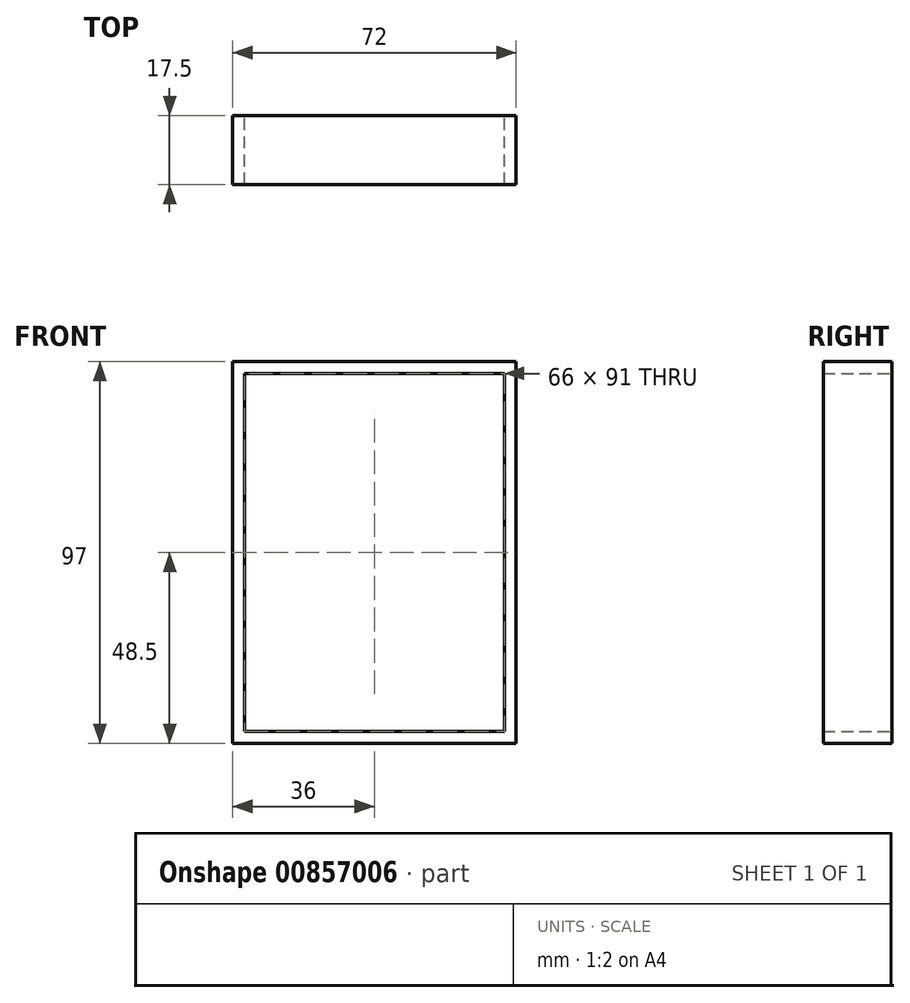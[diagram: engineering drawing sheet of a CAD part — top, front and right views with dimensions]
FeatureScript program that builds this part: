
annotation { "Feature Type Name" : "Feature", "Feature Type Description" : "" }
export const myFeature = defineFeature(function(context is Context, id is Id, definition is map)
    precondition{}
    {
        {
            var Q0;
            Q0=qCreatedBy(makeId("Front.planeOp"),FACE);
            var sketch = newSketch(context, id + "F0", { "sketchPlane" : qUnion([Q0])});
            skLineSegment(sketch, "E0.bottom", {"start": v(33, 45.5) * mm, "end": v(-33, 45.5) * mm});
            skLineSegment(sketch, "E0.top", {"start": v(33, -45.5) * mm, "end": v(-33, -45.5) * mm});
            skLineSegment(sketch, "E0.left", {"start": v(33, 45.5) * mm, "end": v(33, -45.5) * mm});
            skLineSegment(sketch, "E0.right", {"start": v(-33, 45.5) * mm, "end": v(-33, -45.5) * mm});
            skPoint(sketch, "E0.middle", {"position": v(0, 0) * mm});
            skLineSegment(sketch, "E1.0", {"start": v(36, 48.5) * mm, "end": v(-36, 48.5) * mm});
            skLineSegment(sketch, "E1.1", {"start": v(36, 48.5) * mm, "end": v(36, -48.5) * mm});
            skLineSegment(sketch, "E1.2", {"start": v(36, -48.5) * mm, "end": v(-36, -48.5) * mm});
            skLineSegment(sketch, "E1.3", {"start": v(-36, 48.5) * mm, "end": v(-36, -48.5) * mm});
            skSolve(sketch);
        }
        {
            var Q0;
            Q0 = qSketchRegion(id + "F0", true);
            extrude(context, id + "F1", {"entities" : qUnion([Q0]), "endBound" : BoundingType.SYMMETRIC, "depth" : 17.5 * mm, "offsetDistance" : 25 * mm});
        }
    });
